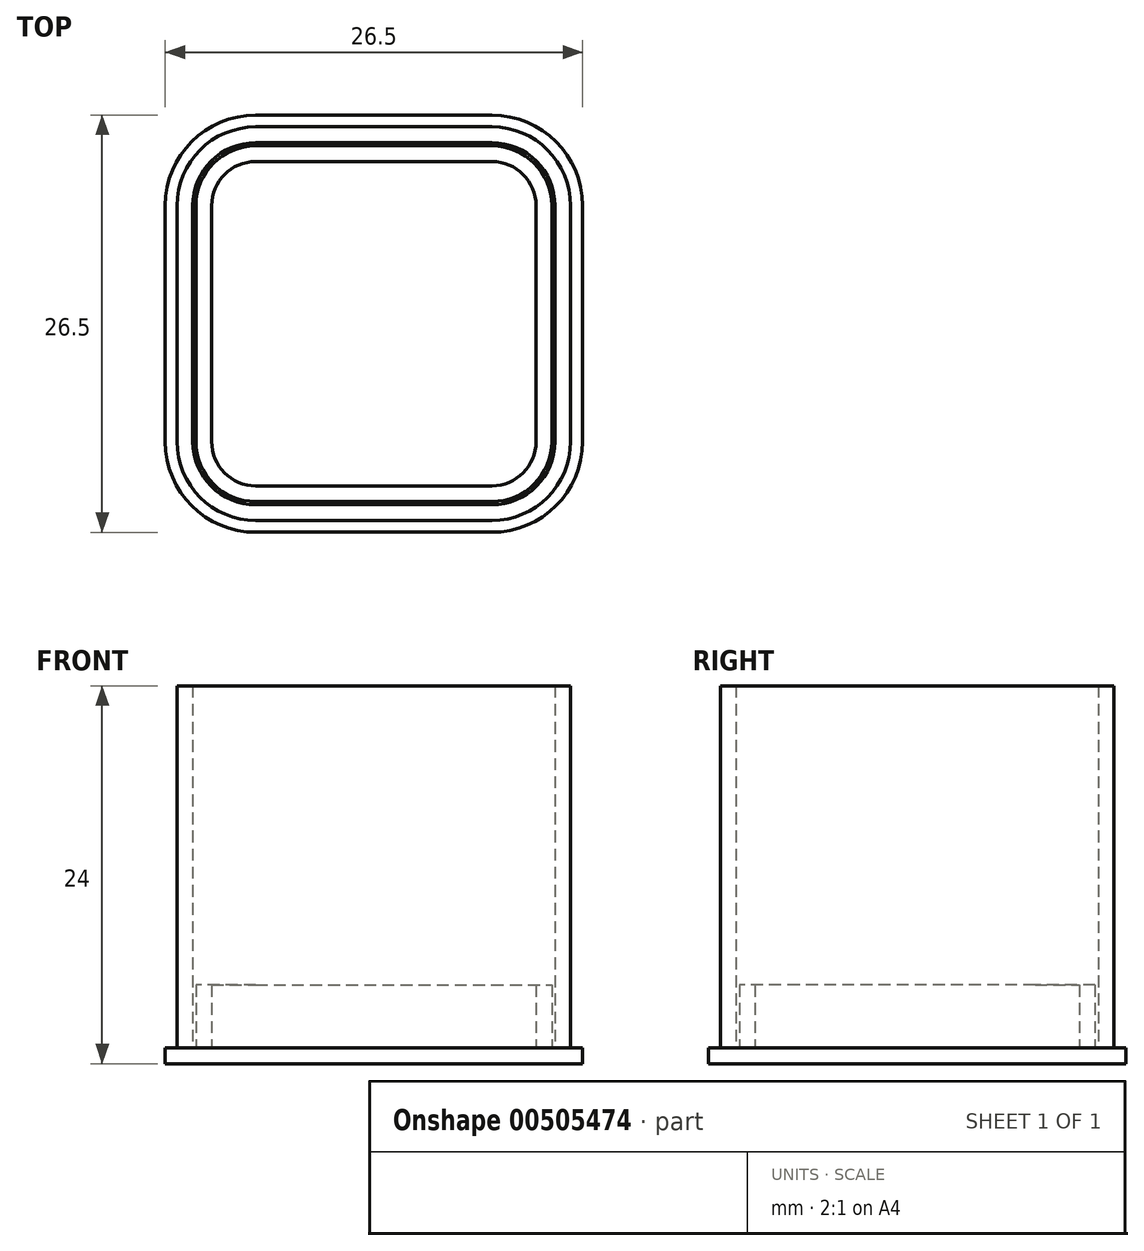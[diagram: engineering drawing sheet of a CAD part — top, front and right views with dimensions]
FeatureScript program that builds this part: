
annotation { "Feature Type Name" : "Feature", "Feature Type Description" : "" }
export const myFeature = defineFeature(function(context is Context, id is Id, definition is map)
    precondition{}
    {
        {
            assignVariable(context, id + "F0", {"name" : "Depth", "anyValue" : 25 * mm});
        }
        {
            assignVariable(context, id + "F1", {"name" : "WallThickness", "anyValue" : 1 * mm});
        }
        {
            assignVariable(context, id + "F2", {"name" : "LidDepth", "anyValue" : 4 * mm});
        }
        {
            var Q0;
            Q0=qCreatedBy(makeId("Top.planeOp"),FACE);
            var sketch = newSketch(context, id + "F3", { "sketchPlane" : qUnion([Q0])});
            skLineSegment(sketch, "E0.bottom", {"start": v(-8.35, 9.1) * mm, "end": v(6.65, 9.1) * mm});
            skLineSegment(sketch, "E0.top", {"start": v(-8.35, -15.9) * mm, "end": v(6.65, -15.9) * mm});
            skLineSegment(sketch, "E0.left", {"start": v(-13.35, 4.1) * mm, "end": v(-13.35, -10.9) * mm});
            skLineSegment(sketch, "E0.right", {"start": v(11.65, 4.1) * mm, "end": v(11.65, -10.9) * mm});
            skPoint(sketch, "E1.visualSharp", {"position": v(-13.35, 9.1) * mm});
            skArc(sketch, "E1.filletArc", {"start": v(-8.35, 9.1) * mm, "mid": v(-11.89, 7.64) * mm, "end": v(-13.35, 4.1) * mm});
            skPoint(sketch, "E2.visualSharp", {"position": v(11.65, 9.1) * mm});
            skArc(sketch, "E2.filletArc", {"start": v(11.65, 4.1) * mm, "mid": v(10.18, 7.64) * mm, "end": v(6.65, 9.1) * mm});
            skPoint(sketch, "E3.visualSharp", {"position": v(11.65, -15.9) * mm});
            skArc(sketch, "E3.filletArc", {"start": v(6.65, -15.9) * mm, "mid": v(10.18, -14.43) * mm, "end": v(11.65, -10.9) * mm});
            skPoint(sketch, "E4.visualSharp", {"position": v(-13.35, -15.9) * mm});
            skArc(sketch, "E4.filletArc", {"start": v(-13.35, -10.9) * mm, "mid": v(-11.89, -14.43) * mm, "end": v(-8.35, -15.9) * mm});
            skArc(sketch, "E5.0", {"start": v(-8.35, 8.1) * mm, "mid": v(-11.18, 6.93) * mm, "end": v(-12.35, 4.1) * mm});
            skLineSegment(sketch, "E5.1", {"start": v(-12.35, 4.1) * mm, "end": v(-12.35, -10.9) * mm});
            skLineSegment(sketch, "E5.2", {"start": v(-8.35, 8.1) * mm, "end": v(6.65, 8.1) * mm});
            skArc(sketch, "E5.3", {"start": v(-12.35, -10.9) * mm, "mid": v(-11.18, -13.72) * mm, "end": v(-8.35, -14.9) * mm});
            skArc(sketch, "E5.4", {"start": v(10.65, 4.1) * mm, "mid": v(9.47, 6.93) * mm, "end": v(6.65, 8.1) * mm});
            skLineSegment(sketch, "E5.5", {"start": v(10.65, 4.1) * mm, "end": v(10.65, -10.9) * mm});
            skArc(sketch, "E5.6", {"start": v(6.65, -14.9) * mm, "mid": v(9.47, -13.72) * mm, "end": v(10.65, -10.9) * mm});
            skLineSegment(sketch, "E5.7", {"start": v(-8.35, -14.9) * mm, "end": v(6.65, -14.9) * mm});
            skArc(sketch, "E6.0", {"start": v(-8.35, 7.9) * mm, "mid": v(-11.04, 6.8) * mm, "end": v(-12.15, 4.1) * mm});
            skLineSegment(sketch, "E6.1", {"start": v(-12.15, 4.1) * mm, "end": v(-12.15, -10.9) * mm});
            skLineSegment(sketch, "E6.2", {"start": v(-8.35, 7.9) * mm, "end": v(6.65, 7.9) * mm});
            skArc(sketch, "E6.3", {"start": v(-12.15, -10.9) * mm, "mid": v(-11.04, -13.58) * mm, "end": v(-8.35, -14.7) * mm});
            skArc(sketch, "E6.4", {"start": v(10.45, 4.1) * mm, "mid": v(9.33, 6.8) * mm, "end": v(6.65, 7.9) * mm});
            skLineSegment(sketch, "E6.5", {"start": v(10.45, 4.1) * mm, "end": v(10.45, -10.9) * mm});
            skArc(sketch, "E6.6", {"start": v(6.65, -14.7) * mm, "mid": v(9.33, -13.58) * mm, "end": v(10.45, -10.9) * mm});
            skLineSegment(sketch, "E6.7", {"start": v(-8.35, -14.7) * mm, "end": v(6.65, -14.7) * mm});
            skArc(sketch, "E7.0", {"start": v(-8.35, 6.9) * mm, "mid": v(-10.33, 6.08) * mm, "end": v(-11.15, 4.1) * mm});
            skLineSegment(sketch, "E7.1", {"start": v(-11.15, 4.1) * mm, "end": v(-11.15, -10.9) * mm});
            skLineSegment(sketch, "E7.2", {"start": v(-8.35, 6.9) * mm, "end": v(6.65, 6.9) * mm});
            skArc(sketch, "E7.3", {"start": v(-11.15, -10.9) * mm, "mid": v(-10.33, -12.88) * mm, "end": v(-8.35, -13.7) * mm});
            skArc(sketch, "E7.4", {"start": v(9.45, 4.1) * mm, "mid": v(8.63, 6.08) * mm, "end": v(6.65, 6.9) * mm});
            skLineSegment(sketch, "E7.5", {"start": v(9.45, 4.1) * mm, "end": v(9.45, -10.9) * mm});
            skArc(sketch, "E7.6", {"start": v(6.65, -13.7) * mm, "mid": v(8.63, -12.88) * mm, "end": v(9.45, -10.9) * mm});
            skLineSegment(sketch, "E7.7", {"start": v(-8.35, -13.7) * mm, "end": v(6.65, -13.7) * mm});
            skArc(sketch, "E8.0", {"start": v(-8.35, 9.85) * mm, "mid": v(-12.42, 8.17) * mm, "end": v(-14.1, 4.1) * mm});
            skLineSegment(sketch, "E8.1", {"start": v(-14.1, 4.1) * mm, "end": v(-14.1, -10.9) * mm});
            skLineSegment(sketch, "E8.2", {"start": v(-8.35, 9.85) * mm, "end": v(6.65, 9.85) * mm});
            skArc(sketch, "E8.3", {"start": v(-14.1, -10.9) * mm, "mid": v(-12.42, -14.96) * mm, "end": v(-8.35, -16.65) * mm});
            skArc(sketch, "E8.4", {"start": v(12.4, 4.1) * mm, "mid": v(10.71, 8.17) * mm, "end": v(6.65, 9.85) * mm});
            skLineSegment(sketch, "E8.5", {"start": v(12.4, 4.1) * mm, "end": v(12.4, -10.9) * mm});
            skArc(sketch, "E8.6", {"start": v(6.65, -16.65) * mm, "mid": v(10.71, -14.96) * mm, "end": v(12.4, -10.9) * mm});
            skLineSegment(sketch, "E8.7", {"start": v(-8.35, -16.65) * mm, "end": v(6.65, -16.65) * mm});
            skSolve(sketch);
        }
        {
            var Q0;
            Q0=makeQuery(id+"F3.imprint","IMPRINT",FACE,{"disambiguationData":[TD([[makeQuery(id+"F3.imprint","IMPRINT",EDGE,{"derivedFrom":sQuery(id+"F3.wireOp",EDGE,"E7.0")}),1.0]])]});
            var Q1;
            Q1=makeQuery(id+"F3.imprint","IMPRINT",FACE,{"disambiguationData":[TD([[makeQuery(id+"F3.imprint","IMPRINT",EDGE,{"derivedFrom":sQuery(id+"F3.wireOp",EDGE,"E6.0")}),1.0]])]});
            var Q2;
            Q2=makeQuery(id+"F3.imprint","IMPRINT",FACE,{"disambiguationData":[TD([[makeQuery(id+"F3.imprint","IMPRINT",EDGE,{"derivedFrom":sQuery(id+"F3.wireOp",EDGE,"E5.0")}),1.0]])]});
            var Q3;
            Q3=makeQuery(id+"F3.imprint","IMPRINT",FACE,{"disambiguationData":[TD([[makeQuery(id+"F3.imprint","IMPRINT",EDGE,{"derivedFrom":sQuery(id+"F3.wireOp",EDGE,"E0.bottom")}),-1.0]])]});
            extrude(context, id + "F4", {"entities" : qUnion([Q0, Q1, Q2, Q3]), "depth" : getVariable(context, 'WallThickness')});
        }
        {
            var Q0;
            Q0=makeQuery(id+"F3.imprint","IMPRINT",FACE,{"disambiguationData":[TD([[makeQuery(id+"F3.imprint","IMPRINT",EDGE,{"derivedFrom":sQuery(id+"F3.wireOp",EDGE,"E0.bottom")}),-1.0]])]});
            extrude(context, id + "F5", {"entities" : qUnion([Q0]), "operationType" : NewBodyOperationType.ADD, "depth" : getVariable(context, 'Depth') - getVariable(context, 'WallThickness')});
        }
        {
            var Q0;
            Q0=makeQuery(id+"F3.imprint","IMPRINT",FACE,{"disambiguationData":[TD([[makeQuery(id+"F3.imprint","IMPRINT",EDGE,{"derivedFrom":sQuery(id+"F3.wireOp",EDGE,"E7.0")}),1.0]])]});
            var Q1;
            Q1=makeQuery(id+"F3.imprint","IMPRINT",FACE,{"disambiguationData":[TD([[makeQuery(id+"F3.imprint","IMPRINT",EDGE,{"derivedFrom":sQuery(id+"F3.wireOp",EDGE,"E6.0")}),1.0]])]});
            var Q2;
            Q2=makeQuery(id+"F3.imprint","IMPRINT",FACE,{"disambiguationData":[TD([[makeQuery(id+"F3.imprint","IMPRINT",EDGE,{"derivedFrom":sQuery(id+"F3.wireOp",EDGE,"E5.0")}),1.0]])]});
            var Q3;
            Q3=makeQuery(id+"F3.imprint","IMPRINT",FACE,{"disambiguationData":[TD([[makeQuery(id+"F3.imprint","IMPRINT",EDGE,{"derivedFrom":sQuery(id+"F3.wireOp",EDGE,"E0.bottom")}),-1.0]])]});
            var Q4;
            Q4=makeQuery(id+"F3.imprint","IMPRINT",FACE,{"disambiguationData":[TD([[makeQuery(id+"F3.imprint","IMPRINT",EDGE,{"derivedFrom":sQuery(id+"F3.wireOp",EDGE,"E0.bottom")}),1.0]])]});
            extrude(context, id + "F6", {"entities" : qUnion([Q0, Q1, Q2, Q3, Q4]), "depth" : getVariable(context, 'WallThickness')});
        }
        {
            var Q0;
            Q0=makeQuery(id+"F3.imprint","IMPRINT",FACE,{"disambiguationData":[TD([[makeQuery(id+"F3.imprint","IMPRINT",EDGE,{"derivedFrom":sQuery(id+"F3.wireOp",EDGE,"E6.0")}),1.0]])]});
            extrude(context, id + "F7", {"entities" : qUnion([Q0]), "operationType" : NewBodyOperationType.ADD, "depth" : getVariable(context, 'WallThickness') + getVariable(context, 'LidDepth')});
        }
    });
